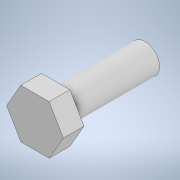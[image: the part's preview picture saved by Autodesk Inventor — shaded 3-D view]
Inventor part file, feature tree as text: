
AUTODESK INVENTOR PART (.ipt)
format: ipt  version: 2022 (Build 260153000, 153)  size: 106,496 bytes
history: native  units: mm
features: extrude x2, sketch x2
ambient origin geometry x8: Origin, YZ Plane, XZ Plane, XY Plane, X Axis, Y Axis, Z Axis, Center Point
bodies: Solid1 (feature_tree)
feature tree (4):
  extrude  "Extrusion1"  Depth=3.9mm TaperAngle=360.0deg
  extrude  "Extrusion2"  Depth=12.3mm
  sketch  "Sketch1"  dims[d0=3.9mm d1=60.0mm d3=360.0deg]
  sketch  "Sketch2"  dims[d5=2.85mm d6=0.0mm d7=4.0mm d8=12.3mm d9=0.0mm]
